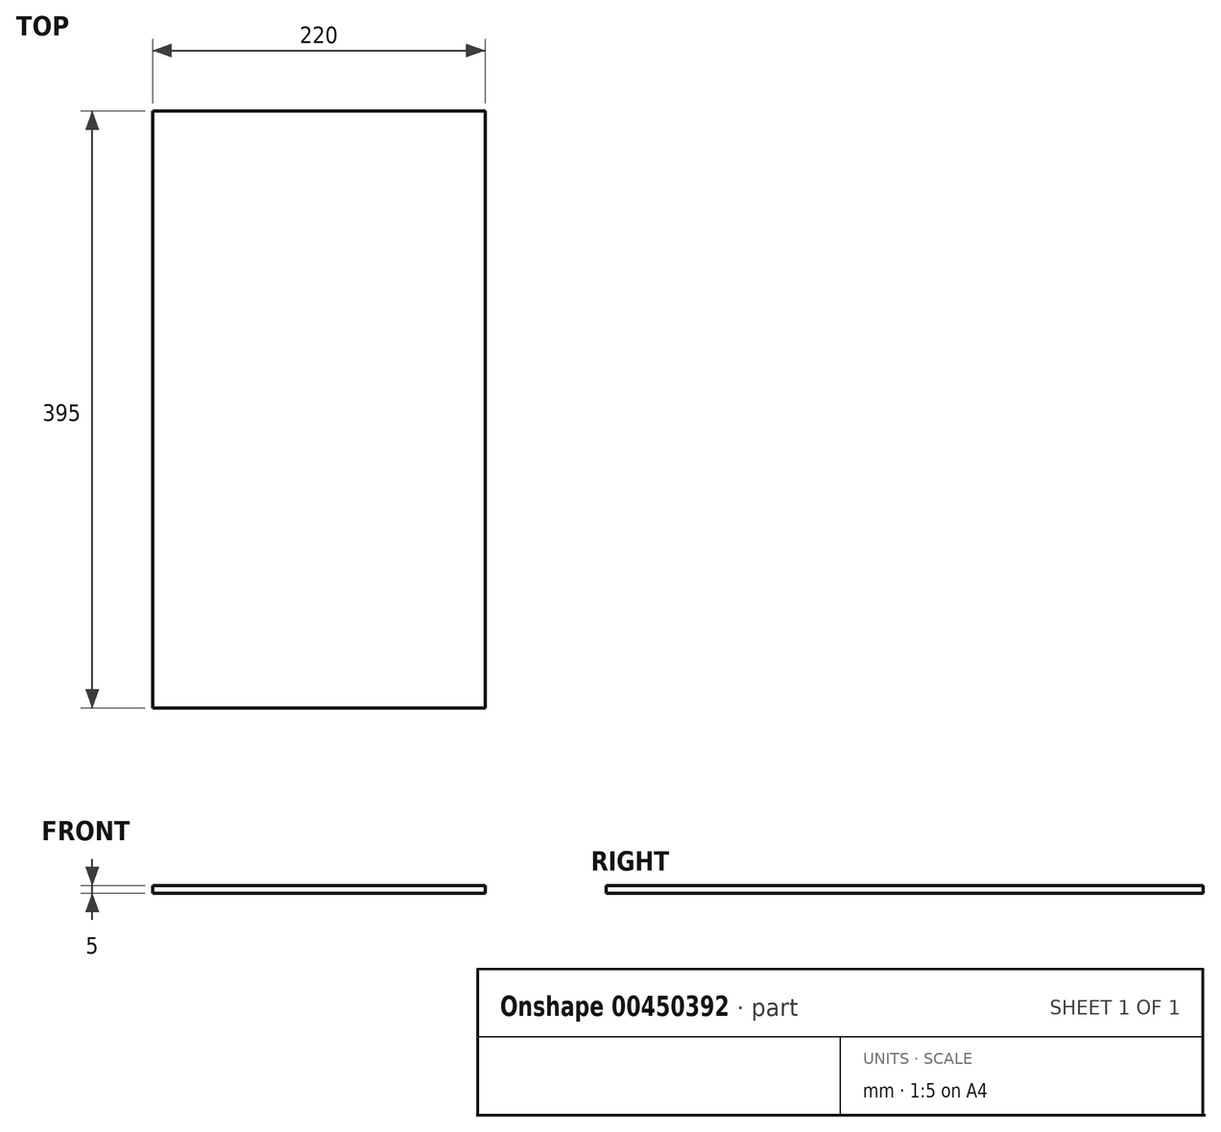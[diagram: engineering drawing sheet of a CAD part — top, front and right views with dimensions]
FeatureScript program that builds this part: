
annotation { "Feature Type Name" : "Feature", "Feature Type Description" : "" }
export const myFeature = defineFeature(function(context is Context, id is Id, definition is map)
    precondition{}
    {
        {
            assignVariable(context, id + "F0", {"name" : "thickness", "anyValue" : 5 * mm});
        }
        {
            var Q0;
            Q0=qCreatedBy(makeId("Top.planeOp"),FACE);
            var sketch = newSketch(context, id + "F1", { "sketchPlane" : qUnion([Q0])});
            skLineSegment(sketch, "E0.bottom", {"start": v(0, 0) * mm, "end": v(-220, 0) * mm});
            skLineSegment(sketch, "E0.top", {"start": v(0, 395) * mm, "end": v(-220, 395) * mm});
            skLineSegment(sketch, "E0.left", {"start": v(0, 0) * mm, "end": v(0, 395) * mm});
            skLineSegment(sketch, "E0.right", {"start": v(-220, 0) * mm, "end": v(-220, 395) * mm});
            skSolve(sketch);
        }
        {
            var Q0;
            Q0 = qSketchRegion(id + "F1", true);
            extrude(context, id + "F2", {"entities" : qUnion([Q0]), "depth" : getVariable(context, 'thickness')});
        }
    });
